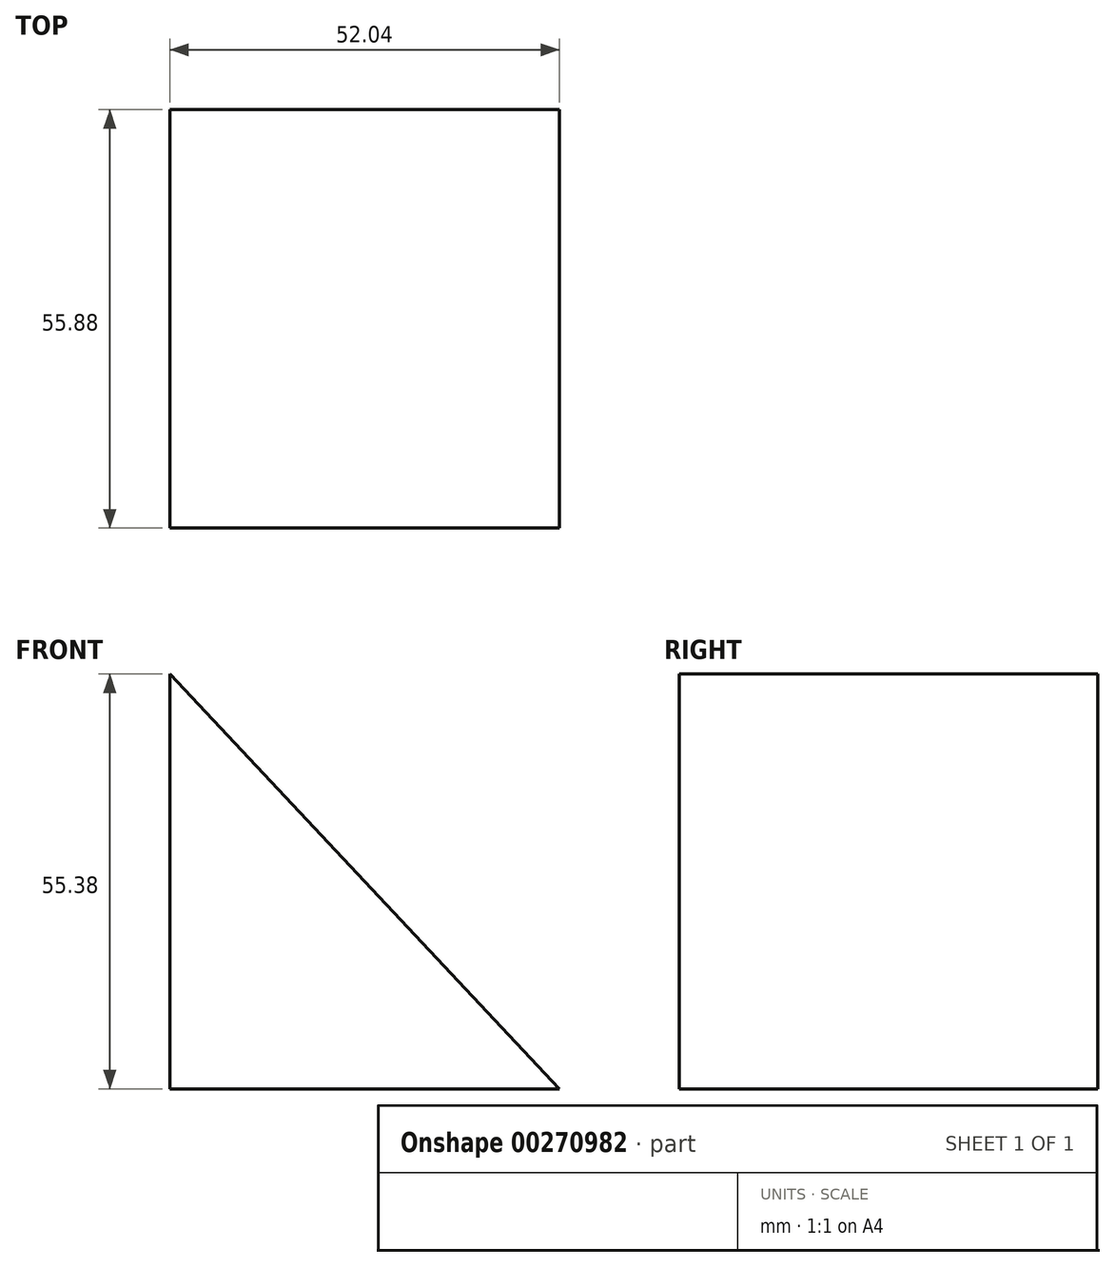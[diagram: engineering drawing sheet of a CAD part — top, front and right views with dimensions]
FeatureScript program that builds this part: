
annotation { "Feature Type Name" : "Feature", "Feature Type Description" : "" }
export const myFeature = defineFeature(function(context is Context, id is Id, definition is map)
    precondition{}
    {
        {
            var Q0;
            Q0=qCreatedBy(makeId("Front.planeOp"),FACE);
            var sketch = newSketch(context, id + "F0", { "sketchPlane" : qUnion([Q0])});
            skLineSegment(sketch, "E0", {"start": v(-52.04, 34.18) * mm, "end": v(-52.04, -21.2) * mm});
            skLineSegment(sketch, "E1", {"start": v(-52.04, -21.2) * mm, "end": v(0, -21.2) * mm});
            skLineSegment(sketch, "E2", {"start": v(-52.04, 34.18) * mm, "end": v(0, -21.2) * mm});
            skSolve(sketch);
        }
        {
            var Q0;
            Q0 = qSketchRegion(id + "F0", true);
            extrude(context, id + "F1", {"entities" : qUnion([Q0]), "depth" : 55.88 * mm});
        }
    });
